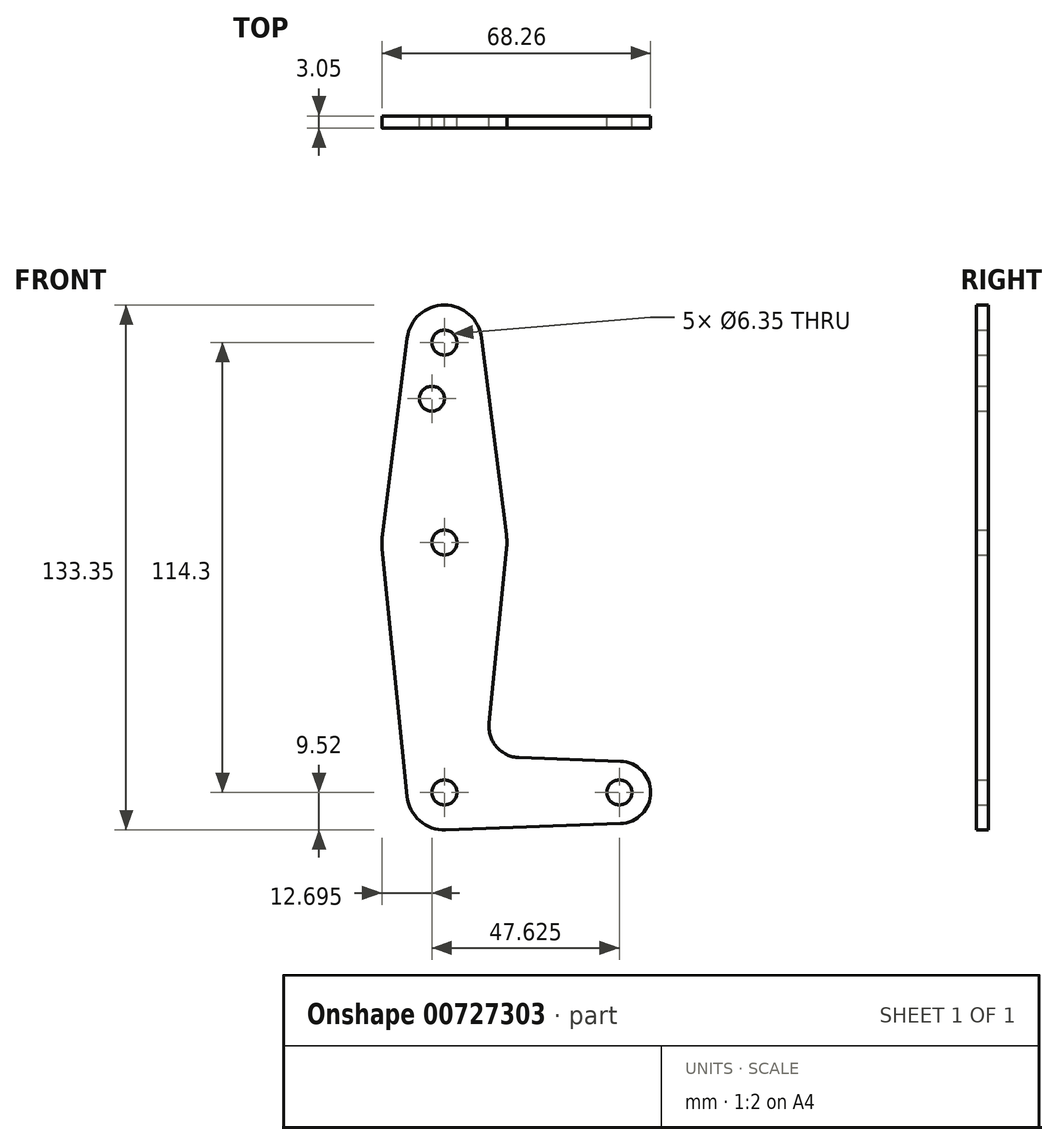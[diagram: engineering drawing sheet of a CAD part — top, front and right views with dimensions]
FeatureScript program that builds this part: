
annotation { "Feature Type Name" : "Feature", "Feature Type Description" : "" }
export const myFeature = defineFeature(function(context is Context, id is Id, definition is map)
    precondition{}
    {
        {
            var Q0;
            Q0=qCreatedBy(makeId("Front.planeOp"),FACE);
            var sketch = newSketch(context, id + "F0", { "sketchPlane" : qUnion([Q0])});
            skLineSegment(sketch, "E0", {"start": v(0, 0) * mm, "end": v(0, 114.3) * mm, "construction": true});
            skLineSegment(sketch, "E1", {"start": v(0, 0) * mm, "end": v(44.45, 0) * mm, "construction": true});
            skArc(sketch, "E2", {"start": v(-9.48, -0.95) * mm, "mid": v(-6.26, -7.18) * mm, "end": v(0.34, -9.52) * mm});
            skArc(sketch, "E3", {"start": v(44.73, -7.93) * mm, "mid": v(52.39, 0) * mm, "end": v(44.73, 7.93) * mm});
            skArc(sketch, "E4", {"start": v(9.45, 115.5) * mm, "mid": v(0, 123.83) * mm, "end": v(-9.45, 115.5) * mm});
            skArc(sketch, "E5", {"start": v(-15.75, 65.48) * mm, "mid": v(-15.87, 63.7) * mm, "end": v(-15.8, 61.91) * mm});
            skLineSegment(sketch, "E6", {"start": v(-9.45, 115.5) * mm, "end": v(-15.75, 65.48) * mm});
            skLineSegment(sketch, "E7", {"start": v(9.45, 115.5) * mm, "end": v(15.75, 65.48) * mm});
            skLineSegment(sketch, "E8", {"start": v(-15.8, 61.91) * mm, "end": v(-9.48, -0.95) * mm});
            skLineSegment(sketch, "E9", {"start": v(18.97, 8.85) * mm, "end": v(44.73, 7.93) * mm});
            skLineSegment(sketch, "E10", {"start": v(0.34, -9.52) * mm, "end": v(44.73, -7.93) * mm});
            skLineSegment(sketch, "E11", {"start": v(15.8, 61.91) * mm, "end": v(11.34, 17.6) * mm});
            skCircle(sketch, "E12", {"center": v(0, 114.3) * mm, "radius": 3.18 * mm});
            skCircle(sketch, "E13", {"center": v(0, 63.5) * mm, "radius": 3.18 * mm});
            skCircle(sketch, "E14", {"center": v(0, 0) * mm, "radius": 3.18 * mm});
            skCircle(sketch, "E15", {"center": v(44.45, 0) * mm, "radius": 3.18 * mm});
            skCircle(sketch, "E16", {"center": v(-3.18, 100.03) * mm, "radius": 3.18 * mm});
            skArc(sketch, "E17.filletArc", {"start": v(11.34, 17.6) * mm, "mid": v(13.26, 11.57) * mm, "end": v(18.97, 8.85) * mm});
            skArc(sketch, "E18.trimOffspring", {"start": v(15.8, 61.91) * mm, "mid": v(15.87, 63.7) * mm, "end": v(15.75, 65.48) * mm});
            skSolve(sketch);
        }
        {
            var Q0;
            Q0 = qSketchRegion(id + "F0", true);
            extrude(context, id + "F1", {"entities" : qUnion([Q0]), "depth" : 3.05 * mm, "offsetDistance" : 25.4 * mm});
        }
    });
